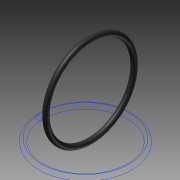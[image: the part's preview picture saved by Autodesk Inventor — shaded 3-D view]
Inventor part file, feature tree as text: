
AUTODESK INVENTOR PART (.ipt)
format: ipt  version: 2012 SP1 (Build 160190100, 190)  size: 124,928 bytes
history: native  units: in
note: dims shown in document units (in); Inventor stores cm internally (conversion verified against a paired STEP export)
features: sketch x2, sweep x1
ambient origin geometry x8: Origin, YZ Plane, XZ Plane, XY Plane, X Axis, Y Axis, Z Axis, Center Point
bodies: Solid1 (feature_tree)
feature tree (3):
  sweep  "Sweep1"
  sketch  "Sketch1"  dims[d0=0.0591in d1=0.9449in]
  sketch  "Sketch2"  dims[d3=0.0in]
